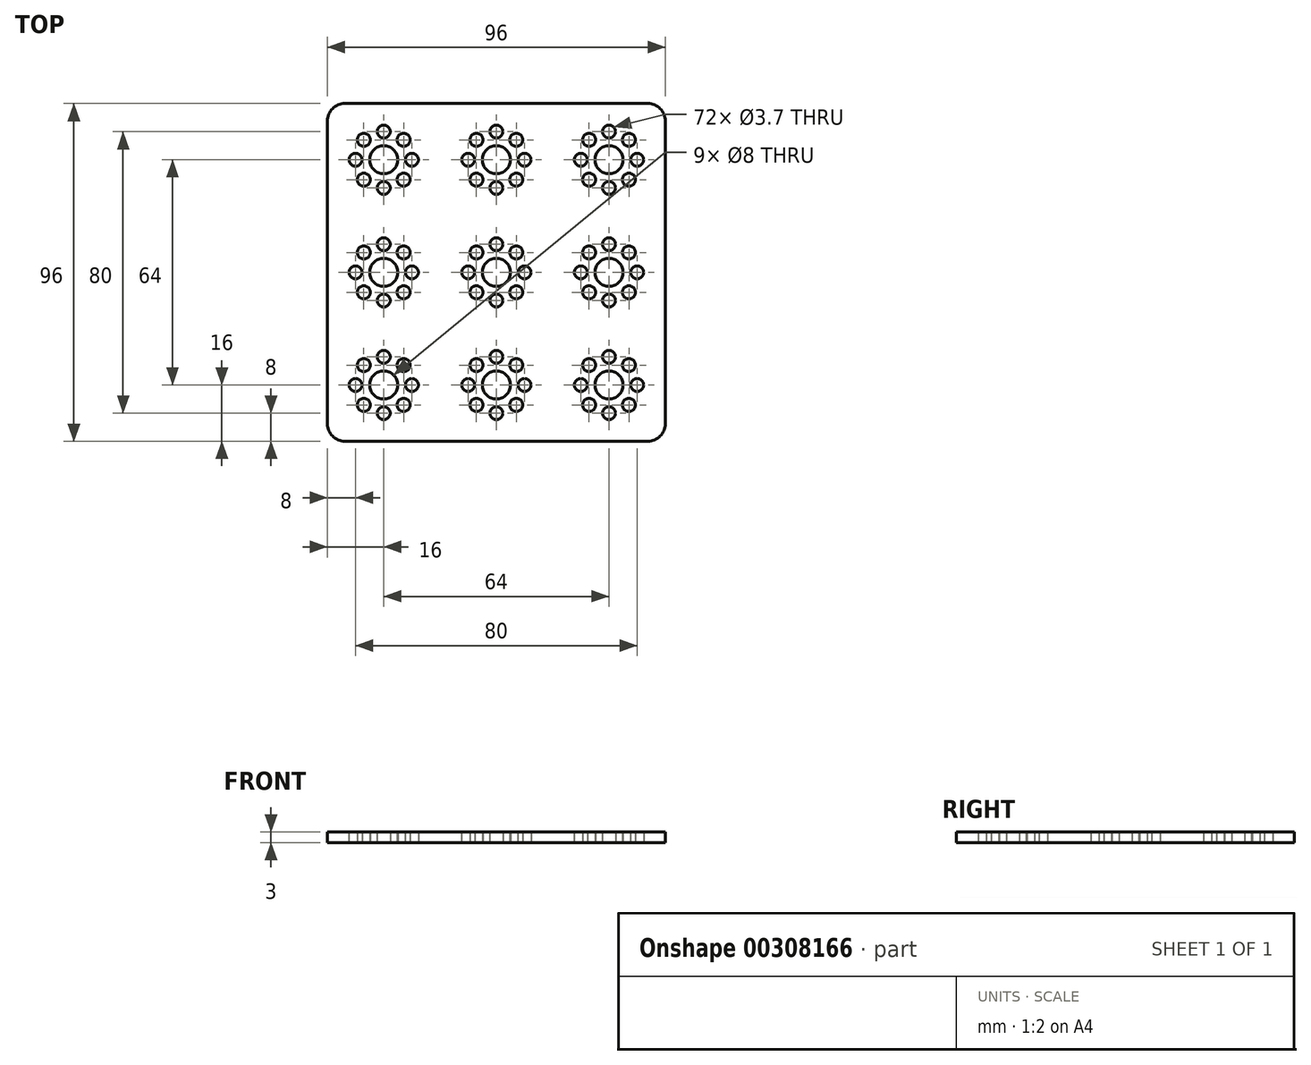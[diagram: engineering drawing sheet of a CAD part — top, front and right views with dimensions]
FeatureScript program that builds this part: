
annotation { "Feature Type Name" : "Feature", "Feature Type Description" : "" }
export const myFeature = defineFeature(function(context is Context, id is Id, definition is map)
    precondition{}
    {
        {
            var Q0;
            Q0=qCreatedBy(makeId("Top.planeOp"),FACE);
            var sketch = newSketch(context, id + "F0", { "sketchPlane" : qUnion([Q0])});
            skLineSegment(sketch, "E0.bottom", {"start": v(5, 96) * mm, "end": v(91, 96) * mm});
            skLineSegment(sketch, "E0.top", {"start": v(5, 0) * mm, "end": v(91, 0) * mm});
            skLineSegment(sketch, "E0.left", {"start": v(0, 91) * mm, "end": v(0, 5) * mm});
            skLineSegment(sketch, "E0.right", {"start": v(96, 91) * mm, "end": v(96, 5) * mm});
            skCircle(sketch, "E1", {"center": v(16, 16) * mm, "radius": 4 * mm});
            skCircle(sketch, "E2", {"center": v(24, 16) * mm, "radius": 1.85 * mm});
            skCircle(sketch, "E3.1.0", {"center": v(21.66, 21.66) * mm, "radius": 1.85 * mm});
            skCircle(sketch, "E3.2.0", {"center": v(16, 24) * mm, "radius": 1.85 * mm});
            skCircle(sketch, "E3.3.0", {"center": v(10.34, 21.66) * mm, "radius": 1.85 * mm});
            skCircle(sketch, "E3.4.0", {"center": v(8, 16) * mm, "radius": 1.85 * mm});
            skCircle(sketch, "E3.5.0", {"center": v(10.34, 10.34) * mm, "radius": 1.85 * mm});
            skCircle(sketch, "E3.6.0", {"center": v(16, 8) * mm, "radius": 1.85 * mm});
            skCircle(sketch, "E3.7.0", {"center": v(21.66, 10.34) * mm, "radius": 1.85 * mm});
            skCircle(sketch, "E4.0.1.0", {"center": v(10.34, 42.34) * mm, "radius": 1.85 * mm});
            skCircle(sketch, "E4.0.1.1", {"center": v(16, 40) * mm, "radius": 1.85 * mm});
            skCircle(sketch, "E4.0.1.2", {"center": v(21.66, 42.34) * mm, "radius": 1.85 * mm});
            skCircle(sketch, "E4.0.1.3", {"center": v(8, 48) * mm, "radius": 1.85 * mm});
            skCircle(sketch, "E4.0.1.4", {"center": v(10.34, 53.66) * mm, "radius": 1.85 * mm});
            skCircle(sketch, "E4.0.1.5", {"center": v(16, 56) * mm, "radius": 1.85 * mm});
            skCircle(sketch, "E4.0.1.6", {"center": v(21.66, 53.66) * mm, "radius": 1.85 * mm});
            skCircle(sketch, "E4.0.1.7", {"center": v(24, 48) * mm, "radius": 1.85 * mm});
            skPoint(sketch, "E4.0.1.8", {"position": v(16, 48) * mm});
            skCircle(sketch, "E4.0.1.9", {"center": v(16, 48) * mm, "radius": 4 * mm});
            skCircle(sketch, "E4.0.2.0", {"center": v(10.34, 74.34) * mm, "radius": 1.85 * mm});
            skCircle(sketch, "E4.0.2.1", {"center": v(16, 72) * mm, "radius": 1.85 * mm});
            skCircle(sketch, "E4.0.2.2", {"center": v(21.66, 74.34) * mm, "radius": 1.85 * mm});
            skCircle(sketch, "E4.0.2.3", {"center": v(8, 80) * mm, "radius": 1.85 * mm});
            skCircle(sketch, "E4.0.2.4", {"center": v(10.34, 85.66) * mm, "radius": 1.85 * mm});
            skCircle(sketch, "E4.0.2.5", {"center": v(16, 88) * mm, "radius": 1.85 * mm});
            skCircle(sketch, "E4.0.2.6", {"center": v(21.66, 85.66) * mm, "radius": 1.85 * mm});
            skCircle(sketch, "E4.0.2.7", {"center": v(24, 80) * mm, "radius": 1.85 * mm});
            skPoint(sketch, "E4.0.2.8", {"position": v(16, 80) * mm});
            skCircle(sketch, "E4.0.2.9", {"center": v(16, 80) * mm, "radius": 4 * mm});
            skCircle(sketch, "E4.1.0.0", {"center": v(42.34, 10.34) * mm, "radius": 1.85 * mm});
            skCircle(sketch, "E4.1.0.1", {"center": v(48, 8) * mm, "radius": 1.85 * mm});
            skCircle(sketch, "E4.1.0.2", {"center": v(53.66, 10.34) * mm, "radius": 1.85 * mm});
            skCircle(sketch, "E4.1.0.3", {"center": v(40, 16) * mm, "radius": 1.85 * mm});
            skCircle(sketch, "E4.1.0.4", {"center": v(42.34, 21.66) * mm, "radius": 1.85 * mm});
            skCircle(sketch, "E4.1.0.5", {"center": v(48, 24) * mm, "radius": 1.85 * mm});
            skCircle(sketch, "E4.1.0.6", {"center": v(53.66, 21.66) * mm, "radius": 1.85 * mm});
            skCircle(sketch, "E4.1.0.7", {"center": v(56, 16) * mm, "radius": 1.85 * mm});
            skPoint(sketch, "E4.1.0.8", {"position": v(48, 16) * mm});
            skCircle(sketch, "E4.1.0.9", {"center": v(48, 16) * mm, "radius": 4 * mm});
            skCircle(sketch, "E4.1.1.0", {"center": v(42.34, 42.34) * mm, "radius": 1.85 * mm});
            skCircle(sketch, "E4.1.1.1", {"center": v(48, 40) * mm, "radius": 1.85 * mm});
            skCircle(sketch, "E4.1.1.2", {"center": v(53.66, 42.34) * mm, "radius": 1.85 * mm});
            skCircle(sketch, "E4.1.1.3", {"center": v(40, 48) * mm, "radius": 1.85 * mm});
            skCircle(sketch, "E4.1.1.4", {"center": v(42.34, 53.66) * mm, "radius": 1.85 * mm});
            skCircle(sketch, "E4.1.1.5", {"center": v(48, 56) * mm, "radius": 1.85 * mm});
            skCircle(sketch, "E4.1.1.6", {"center": v(53.66, 53.66) * mm, "radius": 1.85 * mm});
            skCircle(sketch, "E4.1.1.7", {"center": v(56, 48) * mm, "radius": 1.85 * mm});
            skPoint(sketch, "E4.1.1.8", {"position": v(48, 48) * mm});
            skCircle(sketch, "E4.1.1.9", {"center": v(48, 48) * mm, "radius": 4 * mm});
            skCircle(sketch, "E4.1.2.0", {"center": v(42.34, 74.34) * mm, "radius": 1.85 * mm});
            skCircle(sketch, "E4.1.2.1", {"center": v(48, 72) * mm, "radius": 1.85 * mm});
            skCircle(sketch, "E4.1.2.2", {"center": v(53.66, 74.34) * mm, "radius": 1.85 * mm});
            skCircle(sketch, "E4.1.2.3", {"center": v(40, 80) * mm, "radius": 1.85 * mm});
            skCircle(sketch, "E4.1.2.4", {"center": v(42.34, 85.66) * mm, "radius": 1.85 * mm});
            skCircle(sketch, "E4.1.2.5", {"center": v(48, 88) * mm, "radius": 1.85 * mm});
            skCircle(sketch, "E4.1.2.6", {"center": v(53.66, 85.66) * mm, "radius": 1.85 * mm});
            skCircle(sketch, "E4.1.2.7", {"center": v(56, 80) * mm, "radius": 1.85 * mm});
            skPoint(sketch, "E4.1.2.8", {"position": v(48, 80) * mm});
            skCircle(sketch, "E4.1.2.9", {"center": v(48, 80) * mm, "radius": 4 * mm});
            skCircle(sketch, "E4.2.0.0", {"center": v(74.34, 10.34) * mm, "radius": 1.85 * mm});
            skCircle(sketch, "E4.2.0.1", {"center": v(80, 8) * mm, "radius": 1.85 * mm});
            skCircle(sketch, "E4.2.0.2", {"center": v(85.66, 10.34) * mm, "radius": 1.85 * mm});
            skCircle(sketch, "E4.2.0.3", {"center": v(72, 16) * mm, "radius": 1.85 * mm});
            skCircle(sketch, "E4.2.0.4", {"center": v(74.34, 21.66) * mm, "radius": 1.85 * mm});
            skCircle(sketch, "E4.2.0.5", {"center": v(80, 24) * mm, "radius": 1.85 * mm});
            skCircle(sketch, "E4.2.0.6", {"center": v(85.66, 21.66) * mm, "radius": 1.85 * mm});
            skCircle(sketch, "E4.2.0.7", {"center": v(88, 16) * mm, "radius": 1.85 * mm});
            skPoint(sketch, "E4.2.0.8", {"position": v(80, 16) * mm});
            skCircle(sketch, "E4.2.0.9", {"center": v(80, 16) * mm, "radius": 4 * mm});
            skCircle(sketch, "E4.2.1.0", {"center": v(74.34, 42.34) * mm, "radius": 1.85 * mm});
            skCircle(sketch, "E4.2.1.1", {"center": v(80, 40) * mm, "radius": 1.85 * mm});
            skCircle(sketch, "E4.2.1.2", {"center": v(85.66, 42.34) * mm, "radius": 1.85 * mm});
            skCircle(sketch, "E4.2.1.3", {"center": v(72, 48) * mm, "radius": 1.85 * mm});
            skCircle(sketch, "E4.2.1.4", {"center": v(74.34, 53.66) * mm, "radius": 1.85 * mm});
            skCircle(sketch, "E4.2.1.5", {"center": v(80, 56) * mm, "radius": 1.85 * mm});
            skCircle(sketch, "E4.2.1.6", {"center": v(85.66, 53.66) * mm, "radius": 1.85 * mm});
            skCircle(sketch, "E4.2.1.7", {"center": v(88, 48) * mm, "radius": 1.85 * mm});
            skPoint(sketch, "E4.2.1.8", {"position": v(80, 48) * mm});
            skCircle(sketch, "E4.2.1.9", {"center": v(80, 48) * mm, "radius": 4 * mm});
            skCircle(sketch, "E4.2.2.0", {"center": v(74.34, 74.34) * mm, "radius": 1.85 * mm});
            skCircle(sketch, "E4.2.2.1", {"center": v(80, 72) * mm, "radius": 1.85 * mm});
            skCircle(sketch, "E4.2.2.2", {"center": v(85.66, 74.34) * mm, "radius": 1.85 * mm});
            skCircle(sketch, "E4.2.2.3", {"center": v(72, 80) * mm, "radius": 1.85 * mm});
            skCircle(sketch, "E4.2.2.4", {"center": v(74.34, 85.66) * mm, "radius": 1.85 * mm});
            skCircle(sketch, "E4.2.2.5", {"center": v(80, 88) * mm, "radius": 1.85 * mm});
            skCircle(sketch, "E4.2.2.6", {"center": v(85.66, 85.66) * mm, "radius": 1.85 * mm});
            skCircle(sketch, "E4.2.2.7", {"center": v(88, 80) * mm, "radius": 1.85 * mm});
            skPoint(sketch, "E4.2.2.8", {"position": v(80, 80) * mm});
            skCircle(sketch, "E4.2.2.9", {"center": v(80, 80) * mm, "radius": 4 * mm});
            skLineSegment(sketch, "E4.direction1", {"start": v(10.34, 10.34) * mm, "end": v(42.34, 10.34) * mm, "construction": true});
            skLineSegment(sketch, "E4.direction2", {"start": v(10.34, 10.34) * mm, "end": v(10.34, 42.34) * mm, "construction": true});
            skPoint(sketch, "E5.visualSharp", {"position": v(0, 0) * mm});
            skArc(sketch, "E5.filletArc", {"start": v(0, 5) * mm, "mid": v(1.46, 1.46) * mm, "end": v(5, 0) * mm});
            skPoint(sketch, "E6.visualSharp", {"position": v(96, 0) * mm});
            skArc(sketch, "E6.filletArc", {"start": v(91, 0) * mm, "mid": v(94.54, 1.46) * mm, "end": v(96, 5) * mm});
            skPoint(sketch, "E7.visualSharp", {"position": v(96, 96) * mm});
            skArc(sketch, "E7.filletArc", {"start": v(96, 91) * mm, "mid": v(94.54, 94.54) * mm, "end": v(91, 96) * mm});
            skPoint(sketch, "E8.visualSharp", {"position": v(0, 96) * mm});
            skArc(sketch, "E8.filletArc", {"start": v(5, 96) * mm, "mid": v(1.46, 94.54) * mm, "end": v(0, 91) * mm});
            skSolve(sketch);
        }
        {
            assignVariable(context, id + "F1", {"name" : "thickness", "anyValue" : 3});
        }
        {
            var Q0;
            Q0=makeQuery(id+"F0.imprint","IMPRINT",FACE,{"disambiguationData":[TD([[makeQuery(id+"F0.imprint","IMPRINT",EDGE,{"derivedFrom":sQuery(id+"F0.wireOp",EDGE,"E0.bottom")}),-1.0]])]});
            extrude(context, id + "F2", {"entities" : qUnion([Q0]), "depth" : (getVariable(context, 'thickness')) * mm});
        }
    });
